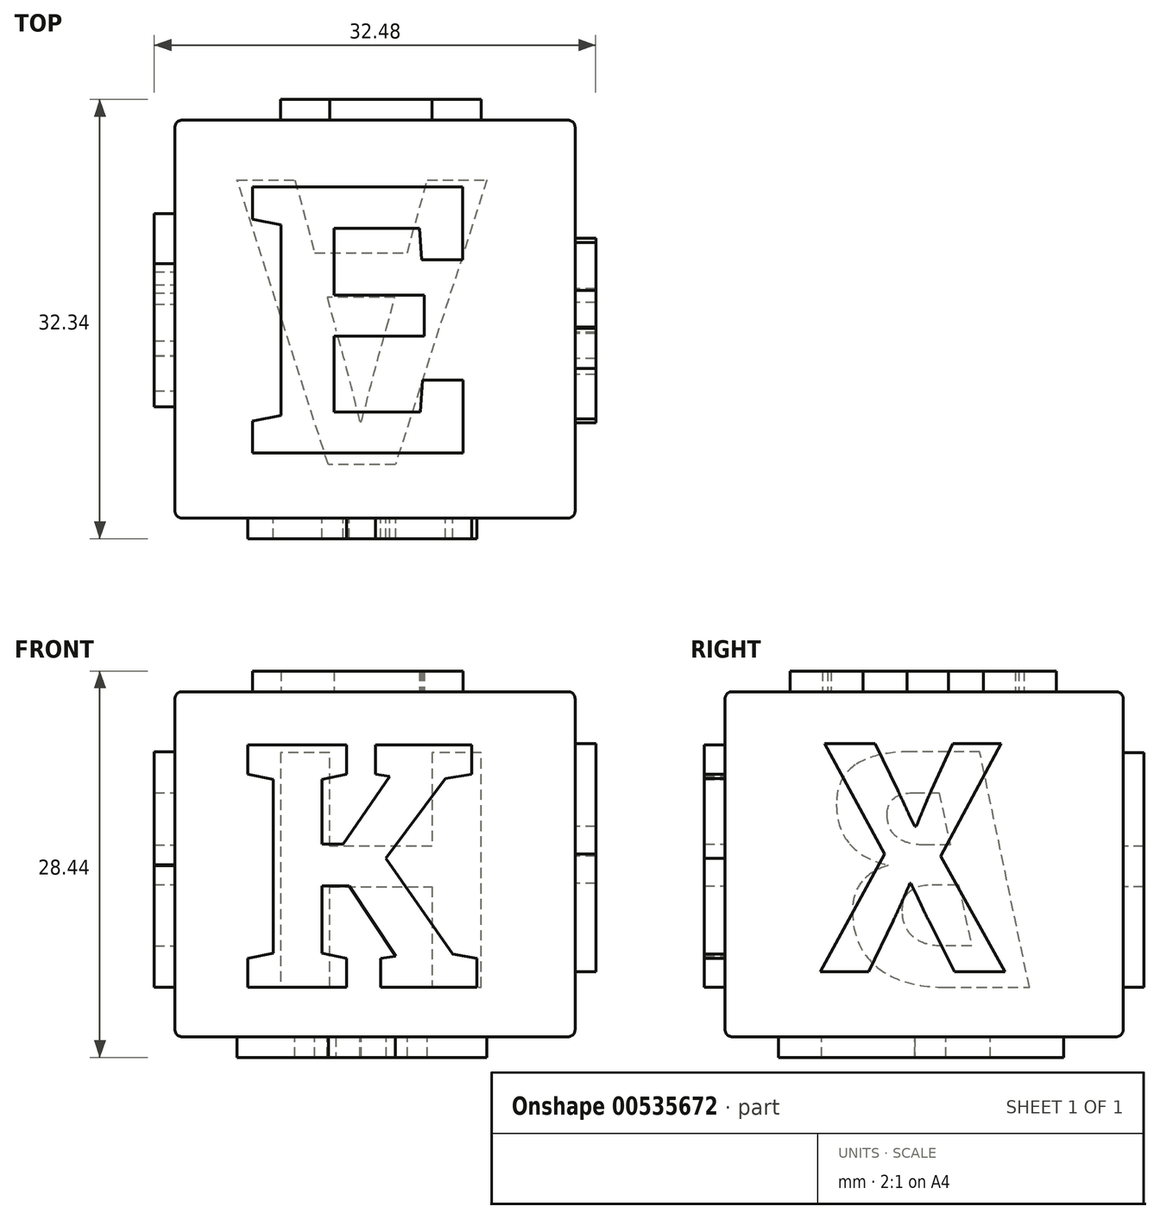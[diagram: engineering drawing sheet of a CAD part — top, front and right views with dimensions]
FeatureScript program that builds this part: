
annotation { "Feature Type Name" : "Feature", "Feature Type Description" : "" }
export const myFeature = defineFeature(function(context is Context, id is Id, definition is map)
    precondition{}
    {
        {
            var Q0;
            Q0=qCreatedBy(makeId("Top.planeOp"),FACE);
            var sketch = newSketch(context, id + "F0", { "sketchPlane" : qUnion([Q0])});
            skLineSegment(sketch, "E0.bottom", {"start": v(0, 0) * mm, "end": v(29.44, 0) * mm});
            skLineSegment(sketch, "E0.top", {"start": v(0, 29.3) * mm, "end": v(29.44, 29.3) * mm});
            skLineSegment(sketch, "E0.left", {"start": v(0, 0) * mm, "end": v(0, 29.3) * mm});
            skLineSegment(sketch, "E0.right", {"start": v(29.44, 0) * mm, "end": v(29.44, 29.3) * mm});
            skSolve(sketch);
        }
        {
            var Q0;
            Q0=makeQuery(id+"F0.imprint","IMPRINT",FACE,{"disambiguationData":[TD([[makeQuery(id+"F0.imprint","IMPRINT",EDGE,{"derivedFrom":sQuery(id+"F0.wireOp",EDGE,"E0.bottom")}),1.0]])]});
            extrude(context, id + "F1", {"entities" : qUnion([Q0]), "depth" : 25.4 * mm, "offsetDistance" : 25.4 * mm});
        }
        {
            var Q0;
            Q0=makeQuery(id+"F1.opExtrude","CAP_FACE",FACE,{"disambiguationData":[OSD([sQuery(id+"F0.wireOp",EDGE,"E0.bottom"),sQuery(id+"F0.wireOp",EDGE,"E0.top"),sQuery(id+"F0.wireOp",EDGE,"E0.left"),sQuery(id+"F0.wireOp",EDGE,"E0.right")])],"isStart":true});
            var sketch = newSketch(context, id + "F2", { "sketchPlane" : qUnion([Q0])});
            skText(sketch, "E1", { "text": "A", "fontName": "NotoSansCJKjp-Bold.otf"});
            const initialGuessF2  = {"E1": [0.00468, -0.0249, 1, 0, 0.0204]};
            skSetInitialGuess(sketch, initialGuessF2);
            skSolve(sketch);
        }
        {
            var Q0;
            Q0=makeQuery(id+"F2.imprint","IMPRINT",FACE,{"disambiguationData":[TD([[makeQuery(id+"F2.imprint","IMPRINT",EDGE,{"derivedFrom":sQuery(id+"F2.wireOp",EDGE,"E1.sketch_text.stroke-0")}),1.0]])]});
            extrude(context, id + "F3", {"entities" : qUnion([Q0]), "operationType" : NewBodyOperationType.ADD, "depth" : 1.52 * mm, "offsetDistance" : 25.4 * mm});
        }
        {
            var Q0;
            Q0=makeQuery(id+"F1.opExtrude","SWEPT_FACE",FACE,{"disambiguationData":[OSD([sQuery(id+"F0.wireOp",EDGE,"E0.right")])]});
            var sketch = newSketch(context, id + "F4", { "sketchPlane" : qUnion([Q0])});
            skText(sketch, "E2", { "text": "X", "fontName": "NotoSansCJKkr-Bold.otf"});
            const initialGuessF4  = {"E2": [0.0067, 0.0048, 1, 0, 0.01632]};
            skSetInitialGuess(sketch, initialGuessF4);
            skSolve(sketch);
        }
        {
            var Q0;
            Q0=makeQuery(id+"F4.imprint","IMPRINT",FACE,{"disambiguationData":[TD([[makeQuery(id+"F4.imprint","IMPRINT",EDGE,{"derivedFrom":sQuery(id+"F4.wireOp",EDGE,"E2.sketch_text.stroke-0")}),1.0]])]});
            extrude(context, id + "F5", {"entities" : qUnion([Q0]), "operationType" : NewBodyOperationType.ADD, "depth" : 1.52 * mm, "offsetDistance" : 25.4 * mm});
        }
        {
            var Q0;
            Q0=makeQuery(id+"F1.opExtrude","SWEPT_FACE",FACE,{"disambiguationData":[OSD([sQuery(id+"F0.wireOp",EDGE,"E0.bottom")])]});
            var sketch = newSketch(context, id + "F6", { "sketchPlane" : qUnion([Q0])});
            skText(sketch, "E3", { "text": "K", "fontName": "RobotoSlab-Bold.ttf"});
            const initialGuessF6  = {"E3": [0.00466, 0.00364, 1, 0, 0.01807]};
            skSetInitialGuess(sketch, initialGuessF6);
            skSolve(sketch);
        }
        {
            var Q0;
            Q0=makeQuery(id+"F6.imprint","IMPRINT",FACE,{"disambiguationData":[TD([[makeQuery(id+"F6.imprint","IMPRINT",EDGE,{"derivedFrom":sQuery(id+"F6.wireOp",EDGE,"E3.sketch_text.stroke-0")}),-1.0]])]});
            extrude(context, id + "F7", {"entities" : qUnion([Q0]), "operationType" : NewBodyOperationType.ADD, "depth" : 1.52 * mm, "offsetDistance" : 25.4 * mm});
        }
        {
            var Q0;
            Q0=makeQuery(id+"F1.opExtrude","SWEPT_FACE",FACE,{"disambiguationData":[OSD([sQuery(id+"F0.wireOp",EDGE,"E0.top")])]});
            var sketch = newSketch(context, id + "F8", { "sketchPlane" : qUnion([Q0])});
            skText(sketch, "E4", { "text": "H", "fontName": "Arimo-Bold.ttf"});
            const initialGuessF8  = {"E4": [-0.0242, 0.00364, 1, 0, 0.01807]};
            skSetInitialGuess(sketch, initialGuessF8);
            skSolve(sketch);
        }
        {
            var Q0;
            Q0=makeQuery(id+"F8.imprint","IMPRINT",FACE,{"disambiguationData":[TD([[makeQuery(id+"F8.imprint","IMPRINT",EDGE,{"derivedFrom":sQuery(id+"F8.wireOp",EDGE,"E4.sketch_text.stroke-0")}),-1.0]])]});
            extrude(context, id + "F9", {"entities" : qUnion([Q0]), "operationType" : NewBodyOperationType.ADD, "depth" : 1.52 * mm, "offsetDistance" : 25.4 * mm});
        }
        {
            var Q0;
            Q0=makeQuery(id+"F1.opExtrude","SWEPT_FACE",FACE,{"disambiguationData":[OSD([sQuery(id+"F0.wireOp",EDGE,"E0.left")])]});
            var sketch = newSketch(context, id + "F10", { "sketchPlane" : qUnion([Q0])});
            skText(sketch, "E5", { "text": "B", "fontName": "OpenSans-BoldItalic.ttf"});
            const initialGuessF10  = {"E5": [-0.02303, 0.00364, 1, 0, 0.01749]};
            skSetInitialGuess(sketch, initialGuessF10);
            skSolve(sketch);
        }
        {
            var Q0;
            Q0=makeQuery(id+"F10.imprint","IMPRINT",FACE,{"disambiguationData":[TD([[makeQuery(id+"F10.imprint","IMPRINT",EDGE,{"derivedFrom":sQuery(id+"F10.wireOp",EDGE,"E5.sketch_text.stroke-0")}),-1.0]])]});
            extrude(context, id + "F11", {"entities" : qUnion([Q0]), "depth" : 1.52 * mm, "offsetDistance" : 25.4 * mm});
        }
        {
            var Q0;
            Q0=makeQuery(id+"F1.opExtrude","CAP_FACE",FACE,{"disambiguationData":[OSD([sQuery(id+"F0.wireOp",EDGE,"E0.bottom"),sQuery(id+"F0.wireOp",EDGE,"E0.top"),sQuery(id+"F0.wireOp",EDGE,"E0.left"),sQuery(id+"F0.wireOp",EDGE,"E0.right")])],"isStart":false});
            var sketch = newSketch(context, id + "F12", { "sketchPlane" : qUnion([Q0])});
            skText(sketch, "E6", { "text": "E", "fontName": "RobotoSlab-Bold.ttf"});
            const initialGuessF12  = {"E6": [0.00496, 0.0048, 1, 0, 0.01982]};
            skSetInitialGuess(sketch, initialGuessF12);
            skSolve(sketch);
        }
        {
            var Q0;
            Q0=makeQuery(id+"F12.imprint","IMPRINT",FACE,{"disambiguationData":[TD([[makeQuery(id+"F12.imprint","IMPRINT",EDGE,{"derivedFrom":sQuery(id+"F12.wireOp",EDGE,"E6.sketch_text.stroke-0")}),-1.0]])]});
            extrude(context, id + "F13", {"entities" : qUnion([Q0]), "operationType" : NewBodyOperationType.ADD, "depth" : 1.52 * mm, "offsetDistance" : 25.4 * mm});
        }
        {
            var Q0;
            Q0=makeQuery(id+"F1.opExtrude","SWEPT_EDGE",EDGE,{"disambiguationData":[OSD([sQuery(id+"F0.wireOp",EDGE,"E0.top"),sQuery(id+"F0.wireOp",EDGE,"E0.left")])]});
            var Q1;
            Q1=makeQuery(id+"F1.opExtrude","CAP_EDGE",EDGE,{"disambiguationData":[OSD([sQuery(id+"F0.wireOp",EDGE,"E0.top")])],"isStart":true});
            var Q2;
            Q2=makeQuery(id+"F1.opExtrude","CAP_EDGE",EDGE,{"disambiguationData":[OSD([sQuery(id+"F0.wireOp",EDGE,"E0.left")])],"isStart":true});
            var Q3;
            Q3=makeQuery(id+"F1.opExtrude","SWEPT_EDGE",EDGE,{"disambiguationData":[OSD([sQuery(id+"F0.wireOp",EDGE,"E0.bottom"),sQuery(id+"F0.wireOp",EDGE,"E0.left")])]});
            var Q4;
            Q4=makeQuery(id+"F1.opExtrude","CAP_EDGE",EDGE,{"disambiguationData":[OSD([sQuery(id+"F0.wireOp",EDGE,"E0.right")])],"isStart":true});
            var Q5;
            Q5=makeQuery(id+"F1.opExtrude","CAP_EDGE",EDGE,{"disambiguationData":[OSD([sQuery(id+"F0.wireOp",EDGE,"E0.bottom")])],"isStart":true});
            var Q6;
            Q6=makeQuery(id+"F1.opExtrude","SWEPT_EDGE",EDGE,{"disambiguationData":[OSD([sQuery(id+"F0.wireOp",EDGE,"E0.bottom"),sQuery(id+"F0.wireOp",EDGE,"E0.right")])]});
            var Q7;
            Q7=makeQuery(id+"F1.opExtrude","CAP_EDGE",EDGE,{"disambiguationData":[OSD([sQuery(id+"F0.wireOp",EDGE,"E0.bottom")])],"isStart":false});
            var Q8;
            Q8=makeQuery(id+"F1.opExtrude","CAP_EDGE",EDGE,{"disambiguationData":[OSD([sQuery(id+"F0.wireOp",EDGE,"E0.left")])],"isStart":false});
            var Q9;
            Q9=makeQuery(id+"F1.opExtrude","CAP_EDGE",EDGE,{"disambiguationData":[OSD([sQuery(id+"F0.wireOp",EDGE,"E0.right")])],"isStart":false});
            var Q10;
            Q10=makeQuery(id+"F1.opExtrude","CAP_EDGE",EDGE,{"disambiguationData":[OSD([sQuery(id+"F0.wireOp",EDGE,"E0.top")])],"isStart":false});
            var Q11;
            Q11=makeQuery(id+"F1.opExtrude","SWEPT_EDGE",EDGE,{"disambiguationData":[OSD([sQuery(id+"F0.wireOp",EDGE,"E0.top"),sQuery(id+"F0.wireOp",EDGE,"E0.right")])]});
            fillet(context, id + "F14", {"entities" : qUnion([Q0, Q1, Q2, Q3, Q4, Q5, Q6, Q7, Q8, Q9, Q10, Q11]), "radius" : 0.5 * mm, "tangentPropagation" : true, "allowEdgeOverflow" : false});
        }
    });
